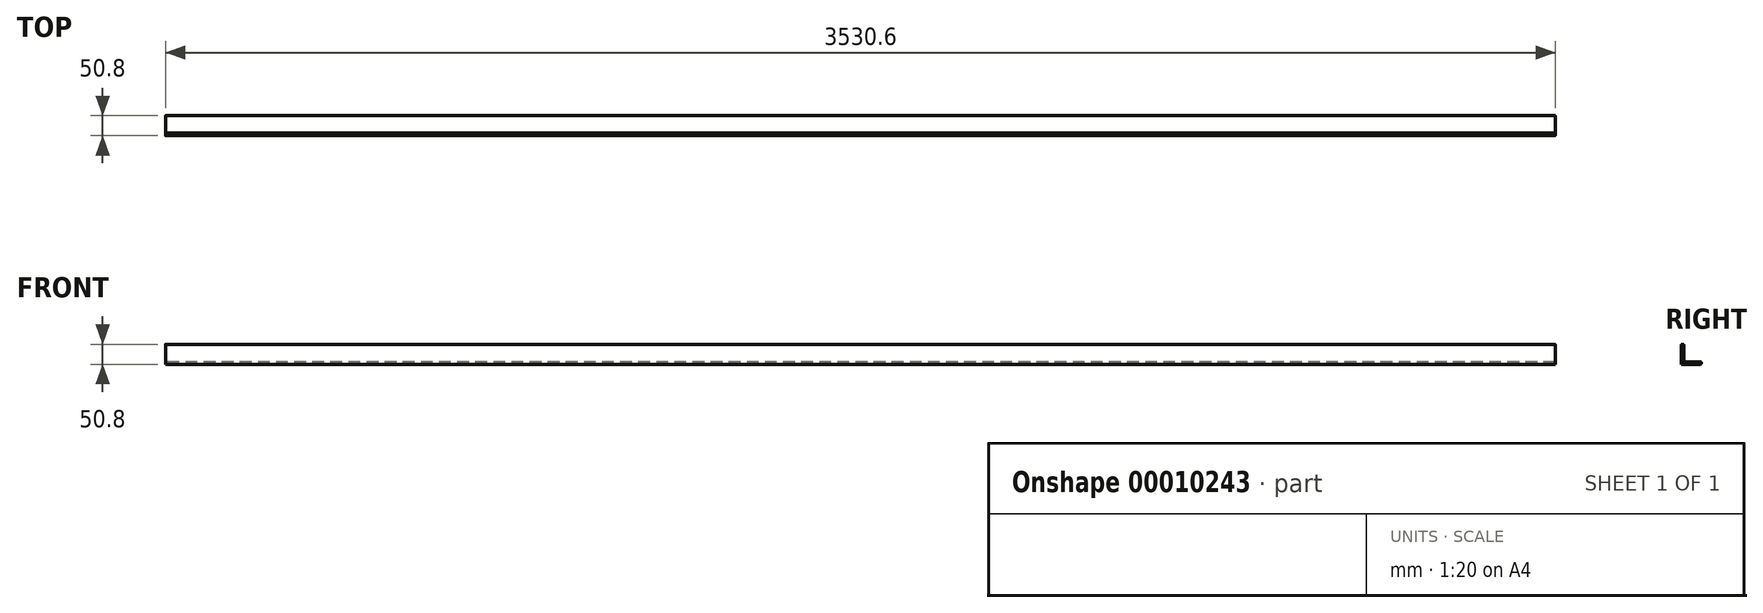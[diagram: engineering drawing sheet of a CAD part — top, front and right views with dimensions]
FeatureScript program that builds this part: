
annotation { "Feature Type Name" : "Feature", "Feature Type Description" : "" }
export const myFeature = defineFeature(function(context is Context, id is Id, definition is map)
    precondition{}
    {
        {
            var Q0;
            Q0=qCreatedBy(makeId("Right.planeOp"),FACE);
            var sketch = newSketch(context, id + "F0", { "sketchPlane" : qUnion([Q0])});
            skLineSegment(sketch, "E0", {"start": v(0, 48.26) * mm, "end": v(0, 0) * mm});
            skLineSegment(sketch, "E1", {"start": v(0, 0) * mm, "end": v(48.26, 0) * mm});
            skLineSegment(sketch, "E2", {"start": v(50.8, 2.54) * mm, "end": v(50.8, 3.81) * mm});
            skLineSegment(sketch, "E3", {"start": v(48.26, 6.35) * mm, "end": v(9.52, 6.35) * mm});
            skLineSegment(sketch, "E4", {"start": v(6.35, 9.52) * mm, "end": v(6.35, 48.26) * mm});
            skLineSegment(sketch, "E5", {"start": v(2.54, 50.8) * mm, "end": v(3.8, 50.8) * mm});
            skPoint(sketch, "E6.visualSharp", {"position": v(6.35, 6.35) * mm});
            skArc(sketch, "E6.filletArc", {"start": v(6.35, 9.52) * mm, "mid": v(7.28, 7.28) * mm, "end": v(9.52, 6.35) * mm});
            skPoint(sketch, "E7.visualSharp", {"position": v(50.8, 6.35) * mm});
            skArc(sketch, "E7.filletArc", {"start": v(50.8, 3.81) * mm, "mid": v(50.06, 5.6) * mm, "end": v(48.26, 6.35) * mm});
            skPoint(sketch, "E8.visualSharp", {"position": v(6.35, 50.8) * mm});
            skArc(sketch, "E8.filletArc", {"start": v(6.35, 48.26) * mm, "mid": v(5.6, 50.06) * mm, "end": v(3.8, 50.8) * mm});
            skPoint(sketch, "E9.visualSharp", {"position": v(0, 50.8) * mm});
            skArc(sketch, "E9.filletArc", {"start": v(2.54, 50.8) * mm, "mid": v(0.74, 50.06) * mm, "end": v(0, 48.26) * mm});
            skPoint(sketch, "E10.visualSharp", {"position": v(50.8, 0) * mm});
            skArc(sketch, "E10.filletArc", {"start": v(48.26, 0) * mm, "mid": v(50.06, 0.74) * mm, "end": v(50.8, 2.54) * mm});
            skSolve(sketch);
        }
        {
            var Q0;
            Q0=makeQuery(id+"F0.imprint","IMPRINT",FACE,{"disambiguationData":[TD([[makeQuery(id+"F0.imprint","IMPRINT",EDGE,{"derivedFrom":sQuery(id+"F0.wireOp",EDGE,"E0")}),1.0]])]});
            extrude(context, id + "F1", {"entities" : qUnion([Q0]), "depth" : 3530.6 * mm});
        }
    });
